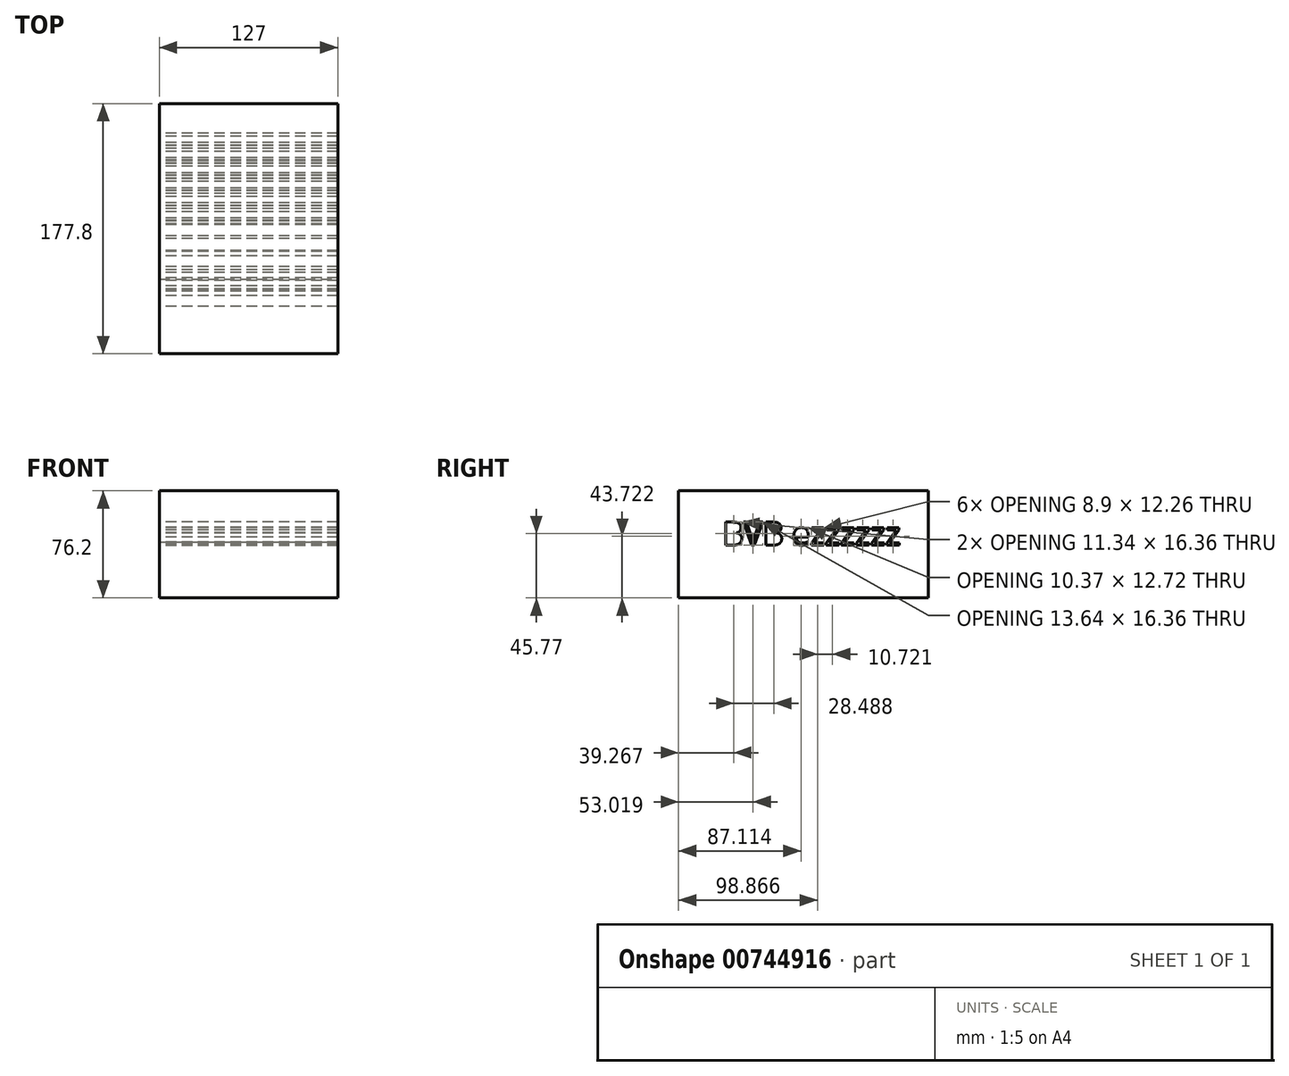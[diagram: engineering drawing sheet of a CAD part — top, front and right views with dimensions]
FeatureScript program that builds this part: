
annotation { "Feature Type Name" : "Feature", "Feature Type Description" : "" }
export const myFeature = defineFeature(function(context is Context, id is Id, definition is map)
    precondition{}
    {
        {
            var Q0;
            Q0=qCreatedBy(makeId("Right.planeOp"),FACE);
            var sketch = newSketch(context, id + "F0", { "sketchPlane" : qUnion([Q0])});
            skLineSegment(sketch, "E0.bottom", {"start": v(-95.75, 30.2) * mm, "end": v(82.05, 30.2) * mm});
            skLineSegment(sketch, "E0.top", {"start": v(-95.75, -46) * mm, "end": v(82.05, -46) * mm});
            skLineSegment(sketch, "E0.left", {"start": v(-95.75, 30.2) * mm, "end": v(-95.75, -46) * mm});
            skLineSegment(sketch, "E0.right", {"start": v(82.05, 30.2) * mm, "end": v(82.05, -46) * mm});
            skText(sketch, "E1", { "text": "BVB ezzzzzz", "fontName": "OpenSans-Regular.ttf"});
            const initialGuessF0  = {"E1": [-0.0644, -0.00842, 1, 0, 0.0165]};
            skSetInitialGuess(sketch, initialGuessF0);
            skSolve(sketch);
        }
        {
            var Q0;
            Q0 = qSketchRegion(id + "F0", true);
            extrude(context, id + "F1", {"entities" : qUnion([Q0]), "endBound" : BoundingType.SYMMETRIC, "depth" : 127 * mm, "offsetDistance" : 25.4 * mm});
        }
    });
